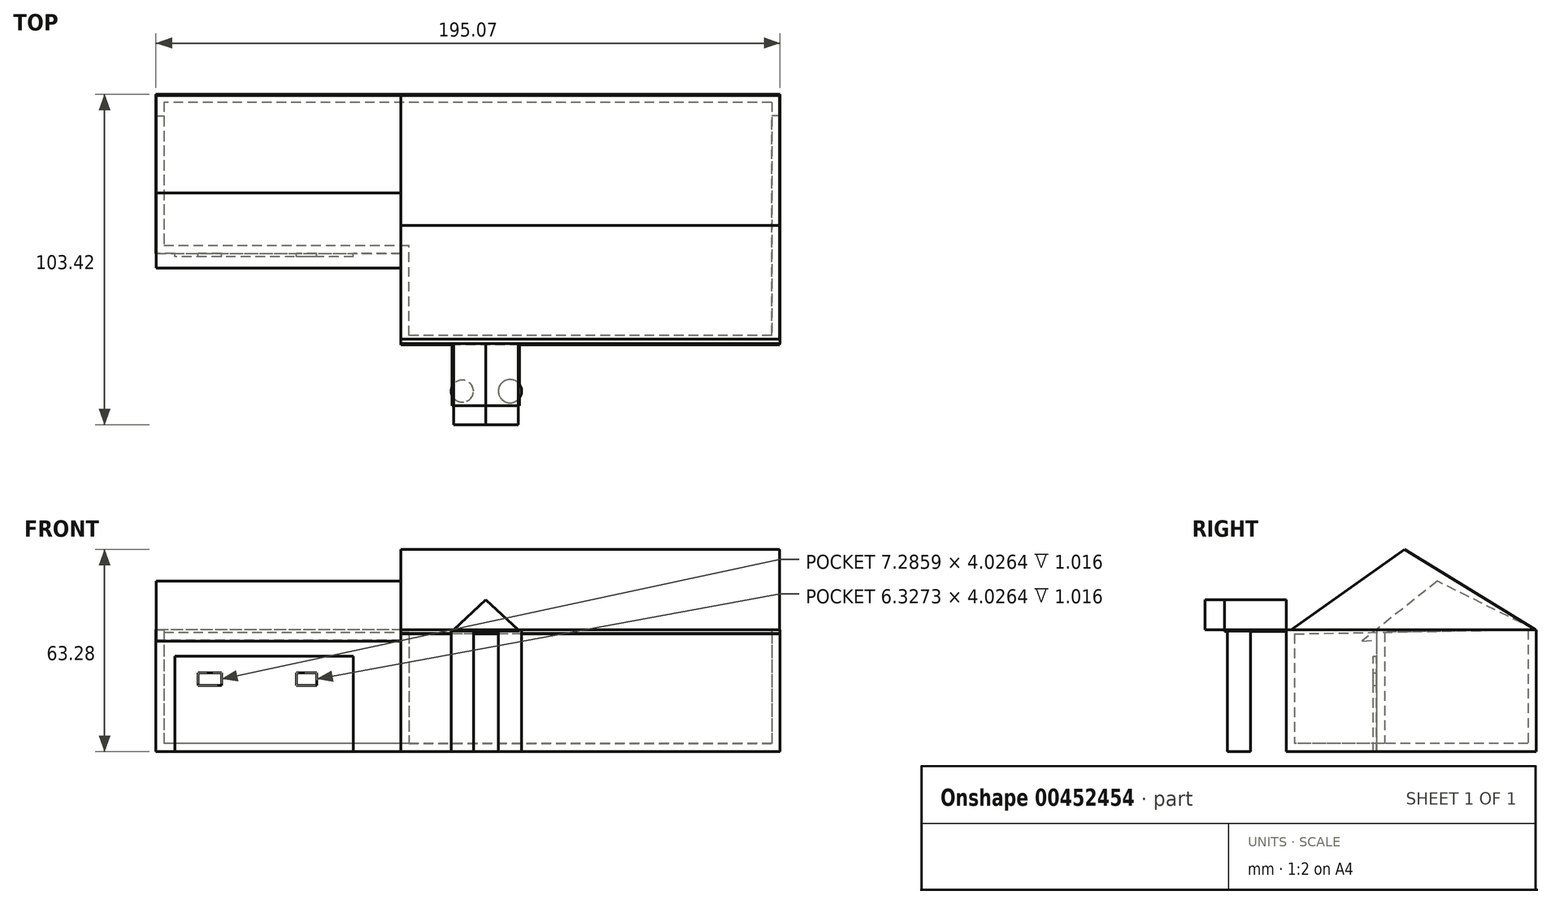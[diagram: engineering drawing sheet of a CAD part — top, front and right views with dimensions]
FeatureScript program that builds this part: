
annotation { "Feature Type Name" : "Feature", "Feature Type Description" : "" }
export const myFeature = defineFeature(function(context is Context, id is Id, definition is map)
    precondition{}
    {
        {
            var Q0;
            Q0=qCreatedBy(makeId("Top.planeOp"),FACE);
            var sketch = newSketch(context, id + "F0", { "sketchPlane" : qUnion([Q0])});
            skLineSegment(sketch, "E0.bottom", {"start": v(0, 49.83) * mm, "end": v(118.57, 49.83) * mm});
            skLineSegment(sketch, "E0.top", {"start": v(0, -28.2) * mm, "end": v(118.57, -28.2) * mm});
            skLineSegment(sketch, "E0.right", {"start": v(118.57, 49.83) * mm, "end": v(118.57, -28.2) * mm});
            skLineSegment(sketch, "E1.bottom", {"start": v(0, 49.83) * mm, "end": v(-76.5, 49.83) * mm});
            skLineSegment(sketch, "E1.top", {"start": v(0, 0) * mm, "end": v(-76.5, 0) * mm});
            skLineSegment(sketch, "E1.right", {"start": v(-76.5, 49.83) * mm, "end": v(-76.5, 0) * mm});
            skLineSegment(sketch, "E2", {"start": v(0, 0) * mm, "end": v(32.61, 0) * mm});
            skLineSegment(sketch, "E3", {"start": v(32.61, 0) * mm, "end": v(32.61, -10.82) * mm});
            skLineSegment(sketch, "E4", {"start": v(32.61, -10.82) * mm, "end": v(36.27, -12.95) * mm});
            skLineSegment(sketch, "E5", {"start": v(36.27, -12.95) * mm, "end": v(34.82, -15.43) * mm});
            skLineSegment(sketch, "E6", {"start": v(34.82, -15.43) * mm, "end": v(30.57, -12.95) * mm});
            skLineSegment(sketch, "E7", {"start": v(30.57, -12.95) * mm, "end": v(30.57, -1.66) * mm});
            skLineSegment(sketch, "E8", {"start": v(30.57, -1.66) * mm, "end": v(2.53, -1.66) * mm});
            skLineSegment(sketch, "E9", {"start": v(2.53, -1.66) * mm, "end": v(2.53, -27.03) * mm});
            skLineSegment(sketch, "E10", {"start": v(2.53, -27.03) * mm, "end": v(30.57, -27.03) * mm});
            skLineSegment(sketch, "E11", {"start": v(30.57, -27.03) * mm, "end": v(30.57, -18) * mm});
            skLineSegment(sketch, "E12", {"start": v(30.57, -18) * mm, "end": v(32.61, -18) * mm});
            skLineSegment(sketch, "E13", {"start": v(32.61, -18) * mm, "end": v(32.61, -28.2) * mm});
            skLineSegment(sketch, "E14", {"start": v(-2.14, 2.84) * mm, "end": v(-73.98, 2.84) * mm});
            skLineSegment(sketch, "E15", {"start": v(-73.98, 2.84) * mm, "end": v(-73.98, 46.16) * mm});
            skLineSegment(sketch, "E16", {"start": v(-73.98, 46.16) * mm, "end": v(-2.14, 46.16) * mm});
            skLineSegment(sketch, "E17", {"start": v(0, 49.83) * mm, "end": v(0, 36.26) * mm});
            skLineSegment(sketch, "E18", {"start": v(0, 36.26) * mm, "end": v(5.01, 33.35) * mm});
            skLineSegment(sketch, "E19", {"start": v(5.01, 33.35) * mm, "end": v(3.93, 31.49) * mm});
            skLineSegment(sketch, "E20", {"start": v(3.93, 31.49) * mm, "end": v(-2.14, 33.35) * mm});
            skLineSegment(sketch, "E21", {"start": v(-2.14, 33.35) * mm, "end": v(-2.14, 46.16) * mm});
            skLineSegment(sketch, "E22", {"start": v(-2.14, 2.84) * mm, "end": v(-2.14, 25.58) * mm});
            skLineSegment(sketch, "E23", {"start": v(-2.14, 25.58) * mm, "end": v(0, 25.58) * mm});
            skLineSegment(sketch, "E24", {"start": v(0, 25.58) * mm, "end": v(0, 0) * mm});
            skLineSegment(sketch, "E25", {"start": v(0, 0) * mm, "end": v(0, -28.2) * mm});
            skLineSegment(sketch, "E26", {"start": v(0, 46.16) * mm, "end": v(115.5, 46.16) * mm});
            skLineSegment(sketch, "E27", {"start": v(115.5, 46.16) * mm, "end": v(115.5, -27.03) * mm});
            skLineSegment(sketch, "E28", {"start": v(115.5, -27.03) * mm, "end": v(32.61, -27.03) * mm});
            skLineSegment(sketch, "E29", {"start": v(79.7, -2.45) * mm, "end": v(79.7, -27.03) * mm});
            skLineSegment(sketch, "E30", {"start": v(79.7, -27.03) * mm, "end": v(81.5, -27.03) * mm});
            skLineSegment(sketch, "E31", {"start": v(81.5, -27.03) * mm, "end": v(81.5, -2.45) * mm});
            skLineSegment(sketch, "E32", {"start": v(48.81, 0) * mm, "end": v(48.81, -10.4) * mm});
            skLineSegment(sketch, "E33", {"start": v(48.81, -10.4) * mm, "end": v(53.68, -8.01) * mm});
            skLineSegment(sketch, "E34", {"start": v(53.68, -8.01) * mm, "end": v(52.74, -6.1) * mm});
            skLineSegment(sketch, "E35", {"start": v(52.74, -6.1) * mm, "end": v(50.7, -7.1) * mm});
            skLineSegment(sketch, "E36", {"start": v(50.7, -7.1) * mm, "end": v(50.7, -2.45) * mm});
            skLineSegment(sketch, "E37", {"start": v(48.81, -27.03) * mm, "end": v(48.81, -15.56) * mm});
            skLineSegment(sketch, "E38", {"start": v(48.81, -15.56) * mm, "end": v(50.7, -15.56) * mm});
            skLineSegment(sketch, "E39", {"start": v(50.7, -15.56) * mm, "end": v(50.7, -28.2) * mm});
            skLineSegment(sketch, "E40", {"start": v(50.7, -2.45) * mm, "end": v(92.61, -2.45) * mm});
            skLineSegment(sketch, "E41", {"start": v(92.61, -2.45) * mm, "end": v(95.58, -7.4) * mm});
            skLineSegment(sketch, "E42", {"start": v(95.58, -7.4) * mm, "end": v(97.44, -6.3) * mm});
            skLineSegment(sketch, "E43", {"start": v(97.44, -6.3) * mm, "end": v(93.67, 0) * mm});
            skLineSegment(sketch, "E44", {"start": v(93.67, 0) * mm, "end": v(48.81, 0) * mm});
            skLineSegment(sketch, "E45", {"start": v(115.5, 0) * mm, "end": v(102.46, 0) * mm});
            skLineSegment(sketch, "E46", {"start": v(102.46, 0) * mm, "end": v(102.46, -2.45) * mm});
            skLineSegment(sketch, "E47", {"start": v(102.46, -2.45) * mm, "end": v(115.5, -2.45) * mm});
            skSolve(sketch);
        }
        {
            var Q0;
            Q0=makeQuery(id+"F0.imprint","IMPRINT",FACE,{"disambiguationData":[TD([[makeQuery(id+"F0.imprint","IMPRINT",EDGE,{"derivedFrom":sQuery(id+"F0.wireOp",EDGE,"E2")}),1.0]])]});
            var Q1;
            {var subQ3=sQuery(id+"F0.wireOp",EDGE,"E1.bottom");Q1=makeQuery(id+"F0.imprint","IMPRINT",FACE,{"disambiguationData":[TD([[makeQuery(id+"F0.imprint","IMPRINT",EDGE,{"derivedFrom":subQ3}),1.0]])]});}
            var Q2;
            Q2=makeQuery(id+"F0.imprint","IMPRINT",FACE,{"disambiguationData":[TD([[makeQuery(id+"F0.imprint","IMPRINT",EDGE,{"derivedFrom":sQuery(id+"F0.wireOp",EDGE,"E2")}),-1.0]])]});
            var Q3;
            {var subQ0=sQuery(id+"F0.wireOp",EDGE,"E37");Q3=makeQuery(id+"F0.imprint","IMPRINT",FACE,{"disambiguationData":[TD([[makeQuery(id+"F0.imprint","IMPRINT",EDGE,{"derivedFrom":subQ0}),-1.0]])]});}
            var Q4;
            {var subQ1=sQuery(id+"F0.wireOp",EDGE,"E13");var subQ6=sQuery(id+"F0.wireOp",EDGE,"E0.top");var subQ7=makeQuery(id+"F0.imprint","INTERSECT",VERTEX,{"derivedFrom":[subQ6,subQ1]});Q4=makeQuery(id+"F0.imprint","IMPRINT",FACE,{"disambiguationData":[TD([[makeQuery(id+"F0.imprint","IMPRINT",EDGE,{"disambiguationData":[TD([[subQ7,-1.0]])],"derivedFrom":subQ6}),1.0]])]});}
            var Q5;
            Q5=makeQuery(id+"F0.imprint","IMPRINT",FACE,{"disambiguationData":[TD([[makeQuery(id+"F0.imprint","IMPRINT",EDGE,{"derivedFrom":sQuery(id+"F0.wireOp",EDGE,"E32")}),1.0]])]});
            var Q6;
            {var subQ0=sQuery(id+"F0.wireOp",EDGE,"E29");Q6=makeQuery(id+"F0.imprint","IMPRINT",FACE,{"disambiguationData":[TD([[makeQuery(id+"F0.imprint","IMPRINT",EDGE,{"derivedFrom":subQ0}),1.0]])]});}
            var Q7;
            {var subQ7=sQuery(id+"F0.wireOp",EDGE,"E0.bottom");Q7=makeQuery(id+"F0.imprint","IMPRINT",FACE,{"disambiguationData":[TD([[makeQuery(id+"F0.imprint","IMPRINT",EDGE,{"derivedFrom":subQ7}),-1.0]])]});}
            var Q8;
            {var subQ0=sQuery(id+"F0.wireOp",EDGE,"E45");Q8=makeQuery(id+"F0.imprint","IMPRINT",FACE,{"disambiguationData":[TD([[makeQuery(id+"F0.imprint","IMPRINT",EDGE,{"derivedFrom":subQ0}),1.0]])]});}
            extrude(context, id + "F1", {"entities" : qUnion([Q0, Q1, Q2, Q3, Q4, Q5, Q6, Q7, Q8]), "depth" : 38.1 * mm});
        }
        {
            var Q0;
            Q0=makeQuery(id+"F1.opExtrude","CAP_FACE",FACE,{"disambiguationData":[OSD([sQuery(id+"F0.wireOp",EDGE,"E0.bottom"),sQuery(id+"F0.wireOp",EDGE,"E0.top"),sQuery(id+"F0.wireOp",EDGE,"E0.right"),sQuery(id+"F0.wireOp",EDGE,"E1.bottom"),sQuery(id+"F0.wireOp",EDGE,"E1.top"),sQuery(id+"F0.wireOp",EDGE,"E1.right"),sQuery(id+"F0.wireOp",EDGE,"E25")])],"isStart":false});
            shell(context, id + "F2", {"entities" : qUnion([Q0]), "thickness" : 2.54 * mm});
        }
        {
            var Q0;
            Q0=qCreatedBy(makeId("Top.planeOp"),FACE);
            var sketch = newSketch(context, id + "F3", { "sketchPlane" : qUnion([Q0])});
            skCircle(sketch, "E48", {"center": v(19.28, -43.07) * mm, "radius": 3.47 * mm});
            skCircle(sketch, "E49", {"center": v(34.19, -43.07) * mm, "radius": 3.65 * mm});
            skSolve(sketch);
        }
        {
            var Q0;
            Q0=makeQuery(id+"F3.imprint","IMPRINT",FACE,{"disambiguationData":[TD([[makeQuery(id+"F3.imprint","IMPRINT",EDGE,{"derivedFrom":sQuery(id+"F3.wireOp",EDGE,"E49")}),1.0]])]});
            var Q1;
            Q1=makeQuery(id+"F3.imprint","IMPRINT",FACE,{"disambiguationData":[TD([[makeQuery(id+"F3.imprint","IMPRINT",EDGE,{"derivedFrom":sQuery(id+"F3.wireOp",EDGE,"E48")}),1.0]])]});
            extrude(context, id + "F4", {"entities" : qUnion([Q0, Q1]), "depth" : 38.1 * mm});
        }
        {
            var Q0;
            Q0=qCreatedBy(makeId("Right.planeOp"),FACE);
            var sketch = newSketch(context, id + "F5", { "sketchPlane" : qUnion([Q0])});
            skLineSegment(sketch, "E50", {"start": v(-28.52, 36.83) * mm, "end": v(8.7, 63.28) * mm});
            skLineSegment(sketch, "E51", {"start": v(8.7, 63.28) * mm, "end": v(49.45, 38.21) * mm});
            skLineSegment(sketch, "E52", {"start": v(49.45, 38.21) * mm, "end": v(-28.52, 36.83) * mm});
            skSolve(sketch);
        }
        {
            var Q0;
            Q0=makeQuery(id+"F5.imprint","IMPRINT",FACE,{"disambiguationData":[TD([[makeQuery(id+"F5.imprint","IMPRINT",EDGE,{"derivedFrom":sQuery(id+"F5.wireOp",EDGE,"E50")}),-1.0]])]});
            extrude(context, id + "F6", {"entities" : qUnion([Q0]), "operationType" : NewBodyOperationType.ADD, "depth" : 118.4 * mm});
        }
        {
            var Q0;
            Q0=qCreatedBy(makeId("Front.planeOp"),FACE);
            var sketch = newSketch(context, id + "F7", { "sketchPlane" : qUnion([Q0])});
            skLineSegment(sketch, "E53", {"start": v(37.3, 37.7) * mm, "end": v(16.12, 37.7) * mm});
            skLineSegment(sketch, "E54", {"start": v(16.12, 37.7) * mm, "end": v(26.7, 47.57) * mm});
            skLineSegment(sketch, "E55", {"start": v(26.7, 47.57) * mm, "end": v(37.3, 37.7) * mm});
            skSolve(sketch);
        }
        {
            var Q0;
            Q0=sQuery(id+"F7.wireOp",EDGE,"E53");
            var Q1;
            Q1=sQuery(id+"F7.wireOp",EDGE,"E55");
            var Q2;
            Q2=sQuery(id+"F7.wireOp",EDGE,"E54");
            extrude(context, id + "F8", {"bodyType" : ToolBodyType.SURFACE, "operationType" : NewBodyOperationType.ADD, "surfaceEntities" : qUnion([Q0, Q1, Q2]), "depth" : 47.5 * mm, "hasDraft" : true, "draftAngle" : 3 * degree});
        }
        {
            var Q0;
            Q0=makeQuery(id+"F6.boolean.opBoolean","MERGE",FACE,{"derivedFrom":[makeQuery(id+"F1.opExtrude","SWEPT_FACE",FACE,{"disambiguationData":[OSD([sQuery(id+"F0.wireOp",EDGE,"E25")])]}),makeQuery(id+"F6.opExtrude","CAP_FACE",FACE,{"disambiguationData":[OSD([sQuery(id+"F5.wireOp",EDGE,"E50"),sQuery(id+"F5.wireOp",EDGE,"E51"),sQuery(id+"F5.wireOp",EDGE,"E52")])],"isStart":true})]});
            var sketch = newSketch(context, id + "F9", { "sketchPlane" : qUnion([Q0])});
            skLineSegment(sketch, "E56", {"start": v(-49.45, 38.21) * mm, "end": v(-18.97, 53.37) * mm});
            skLineSegment(sketch, "E57", {"start": v(-18.97, 53.37) * mm, "end": v(4.61, 34.63) * mm});
            skLineSegment(sketch, "E58", {"start": v(4.61, 34.63) * mm, "end": v(-49.45, 38.21) * mm});
            skSolve(sketch);
        }
        {
            var Q0;
            {var subQ10=sQuery(id+"F9.wireOp",EDGE,"E56");Q0=makeQuery(id+"F9.imprint","IMPRINT",FACE,{"disambiguationData":[TD([[makeQuery(id+"F9.imprint","IMPRINT",EDGE,{"derivedFrom":subQ10}),-1.0]])]});}
            var Q1;
            {var subQ0=sQuery(id+"F9.wireOp",EDGE,"E58");var subQ1=sQuery(id+"F9.wireOp",EDGE,"E57");var subQ2=makeQuery(id+"F9.imprint","INTERSECT",VERTEX,{"derivedFrom":[subQ1,subQ0]});Q1=makeQuery(id+"F9.imprint","IMPRINT",FACE,{"disambiguationData":[TD([[makeQuery(id+"F9.imprint","IMPRINT",EDGE,{"disambiguationData":[TD([[subQ2,1.0]])],"derivedFrom":subQ1}),-1.0]])]});}
            extrude(context, id + "F10", {"entities" : qUnion([Q0, Q1]), "operationType" : NewBodyOperationType.ADD, "depth" : 76.38 * mm});
        }
        {
            var Q0;
            Q0=makeQuery(id+"F1.opExtrude","SWEPT_FACE",FACE,{"disambiguationData":[OSD([sQuery(id+"F0.wireOp",EDGE,"E1.top")])]});
            var sketch = newSketch(context, id + "F11", { "sketchPlane" : qUnion([Q0])});
            skLineSegment(sketch, "E59", {"start": v(-70.57, 0) * mm, "end": v(-70.57, 29.92) * mm});
            skLineSegment(sketch, "E60", {"start": v(-70.57, 29.92) * mm, "end": v(-14.78, 29.92) * mm});
            skLineSegment(sketch, "E61", {"start": v(-14.78, 29.92) * mm, "end": v(-14.78, 0) * mm});
            skLineSegment(sketch, "E62", {"start": v(-14.78, 0) * mm, "end": v(-70.57, 0) * mm});
            skLineSegment(sketch, "E63", {"start": v(-26.28, 24.74) * mm, "end": v(-32.6, 24.74) * mm});
            skLineSegment(sketch, "E64", {"start": v(-32.6, 24.74) * mm, "end": v(-32.6, 20.72) * mm});
            skLineSegment(sketch, "E65", {"start": v(-32.6, 20.72) * mm, "end": v(-26.28, 20.72) * mm});
            skLineSegment(sketch, "E66", {"start": v(-26.28, 20.72) * mm, "end": v(-26.28, 24.74) * mm});
            skLineSegment(sketch, "E67", {"start": v(-56, 24.74) * mm, "end": v(-63.29, 24.74) * mm});
            skLineSegment(sketch, "E68", {"start": v(-63.29, 24.74) * mm, "end": v(-63.29, 20.72) * mm});
            skLineSegment(sketch, "E69", {"start": v(-63.29, 20.72) * mm, "end": v(-56, 20.72) * mm});
            skLineSegment(sketch, "E70", {"start": v(-56, 20.72) * mm, "end": v(-56, 24.74) * mm});
            skSolve(sketch);
        }
        {
            var Q0;
            Q0=makeQuery(id+"F11.imprint","IMPRINT",FACE,{"disambiguationData":[TD([[makeQuery(id+"F11.imprint","IMPRINT",EDGE,{"derivedFrom":sQuery(id+"F11.wireOp",EDGE,"E59")}),-1.0]])]});
            extrude(context, id + "F12", {"entities" : qUnion([Q0]), "operationType" : NewBodyOperationType.ADD, "depth" : 1.02 * mm});
        }
        {
            var Q0;
            Q0=makeQuery(id+"F1.opExtrude","SWEPT_FACE",FACE,{"disambiguationData":[OSD([sQuery(id+"F0.wireOp",EDGE,"E0.top")])]});
            var sketch = newSketch(context, id + "F13", { "sketchPlane" : qUnion([Q0])});
            skLineSegment(sketch, "E71", {"start": v(16.12, 37.7) * mm, "end": v(26.56, 47.55) * mm});
            skLineSegment(sketch, "E72", {"start": v(26.56, 47.55) * mm, "end": v(37.17, 37.77) * mm});
            skLineSegment(sketch, "E73", {"start": v(37.17, 37.77) * mm, "end": v(16.12, 37.7) * mm});
            skSolve(sketch);
        }
        {
            var Q0;
            {var subQ0=sQuery(id+"F13.wireOp",EDGE,"E72");var subQ1=sQuery(id+"F13.wireOp",EDGE,"E71");var subQ2=makeQuery(id+"F13.imprint","INTERSECT",VERTEX,{"derivedFrom":[subQ1,subQ0]});Q0=makeQuery(id+"F13.imprint","IMPRINT",FACE,{"disambiguationData":[TD([[makeQuery(id+"F13.imprint","IMPRINT",EDGE,{"disambiguationData":[TD([[subQ2,1.0]])],"derivedFrom":subQ1}),-1.0]])]});}
            var Q1;
            {var subQ0=sQuery(id+"F13.wireOp",EDGE,"E73");Q1=makeQuery(id+"F13.imprint","IMPRINT",FACE,{"disambiguationData":[TD([[makeQuery(id+"F13.imprint","IMPRINT",EDGE,{"derivedFrom":subQ0}),-1.0]])]});}
            extrude(context, id + "F14", {"entities" : qUnion([Q0, Q1]), "depth" : 19.38 * mm});
        }
        {
            var Q0;
            Q0=qCreatedBy(makeId("Top.planeOp"),FACE);
            var sketch = newSketch(context, id + "F15", { "sketchPlane" : qUnion([Q0])});
            skLineSegment(sketch, "E74.bottom", {"start": v(9.71, 7.82) * mm, "end": v(16.97, 7.82) * mm});
            skLineSegment(sketch, "E74.top", {"start": v(9.71, 2.1) * mm, "end": v(16.97, 2.1) * mm});
            skLineSegment(sketch, "E74.left", {"start": v(9.71, 7.82) * mm, "end": v(9.71, 2.1) * mm});
            skLineSegment(sketch, "E74.right", {"start": v(16.97, 7.82) * mm, "end": v(16.97, 2.1) * mm});
            skSolve(sketch);
        }
        {
            var Q0;
            Q0=sQuery(id+"F15.wireOp",EDGE,"E74.top");
            var Q1;
            Q1=sQuery(id+"F15.wireOp",EDGE,"E74.right");
            var Q2;
            Q2=sQuery(id+"F15.wireOp",EDGE,"E74.bottom");
            var Q3;
            Q3=sQuery(id+"F15.wireOp",EDGE,"E74.left");
            extrude(context, id + "F16", {"bodyType" : ToolBodyType.SURFACE, "surfaceEntities" : qUnion([Q0, Q1, Q2, Q3]), "depth" : 70.1 * mm});
        }
        {
            var Q0;
            {var subQ0=sQuery(id+"F13.wireOp",EDGE,"E72");var subQ1=sQuery(id+"F13.wireOp",EDGE,"E71");var subQ2=makeQuery(id+"F13.imprint","INTERSECT",VERTEX,{"derivedFrom":[subQ1,subQ0]});Q0=makeQuery(id+"F13.imprint","IMPRINT",FACE,{"disambiguationData":[TD([[makeQuery(id+"F13.imprint","IMPRINT",EDGE,{"disambiguationData":[TD([[subQ2,1.0]])],"derivedFrom":subQ1}),-1.0]])]});}
            extrude(context, id + "F17", {"entities" : qUnion([Q0]), "depth" : 25.4 * mm});
        }
    });
